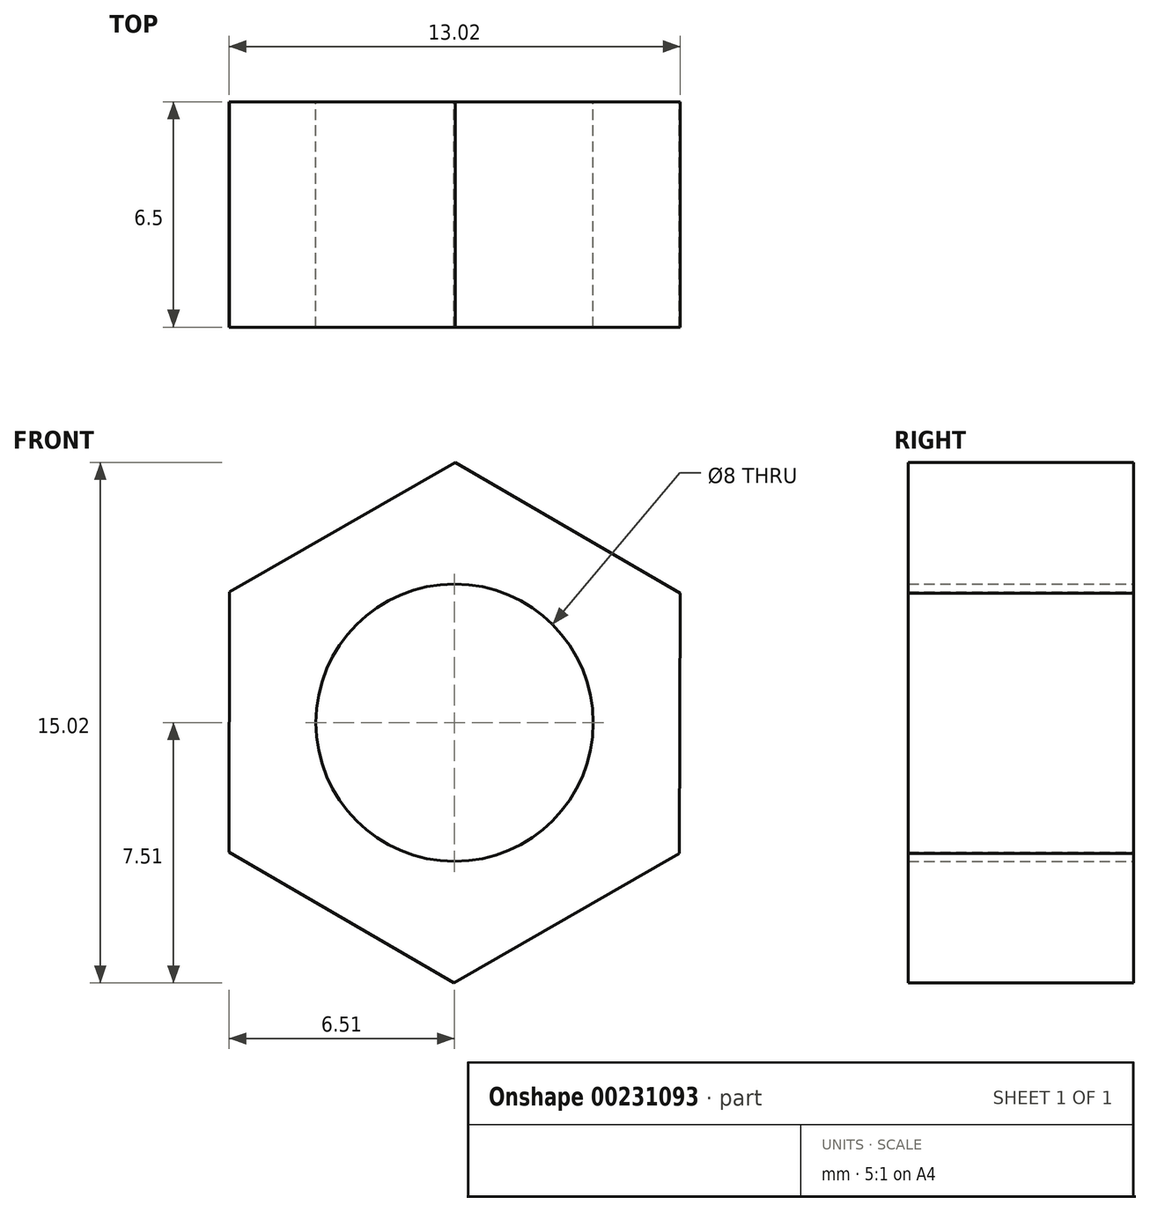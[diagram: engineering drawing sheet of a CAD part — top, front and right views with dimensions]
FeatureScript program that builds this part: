
annotation { "Feature Type Name" : "Feature", "Feature Type Description" : "" }
export const myFeature = defineFeature(function(context is Context, id is Id, definition is map)
    precondition{}
    {
        {
            var Q0;
            Q0=qCreatedBy(makeId("Front.planeOp"),FACE);
            var sketch = newSketch(context, id + "F0", { "sketchPlane" : qUnion([Q0])});
            skCircle(sketch, "E0.cCircle", {"center": v(0, 0) * mm, "radius": 6.5 * mm, "construction": true});
            skLineSegment(sketch, "E0.0", {"start": v(0.02, 7.5) * mm, "end": v(6.51, 3.73) * mm});
            skLineSegment(sketch, "E0.1", {"start": v(6.51, 3.73) * mm, "end": v(6.49, -3.77) * mm});
            skLineSegment(sketch, "E0.2", {"start": v(6.49, -3.77) * mm, "end": v(-0.02, -7.5) * mm});
            skLineSegment(sketch, "E0.3", {"start": v(-0.02, -7.5) * mm, "end": v(-6.51, -3.73) * mm});
            skLineSegment(sketch, "E0.4", {"start": v(-6.51, -3.73) * mm, "end": v(-6.49, 3.77) * mm});
            skLineSegment(sketch, "E0.5", {"start": v(-6.49, 3.77) * mm, "end": v(0.02, 7.5) * mm});
            skPoint(sketch, "E0.0.midPoint", {"position": v(3.27, 5.62) * mm});
            skCircle(sketch, "E1", {"center": v(0, 0) * mm, "radius": 4 * mm});
            skSolve(sketch);
        }
        {
            var Q0;
            Q0 = qSketchRegion(id + "F0", true);
            extrude(context, id + "F1", {"entities" : qUnion([Q0]), "depth" : 6.5 * mm});
        }
    });
